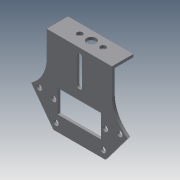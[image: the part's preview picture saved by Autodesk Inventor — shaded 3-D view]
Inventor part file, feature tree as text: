
AUTODESK INVENTOR PART (.ipt)
format: ipt  version: 2013 (Build 170138000, 138)  size: 1,016,832 bytes
history: native  units: mm
features: sketch x90, extrude x79, fillet x2
ambient origin geometry x8: Origin, YZ Plane, XZ Plane, XY Plane, X Axis, Y Axis, Z Axis, Center Point
bodies: Solid1 (feature_tree)
feature tree (171):
  extrude  "Extrusion1"  Depth=10.0mm
  extrude  "Extrusion2"  Depth=10.0mm
  sketch  "Sketch3"  dims[d8=2.0mm d9=0.0mm d11=3.0mm]
  extrude  "Extrusion3"  Depth=3.0mm
  extrude  "Extrusion4"  Depth=3.0mm
  extrude  "Extrusion5"  Depth=10.0mm TaperAngle=0.0deg
  extrude  "Extrusion6"  Depth=3.0mm
  sketch  "Sketch8"  dims[d24=10.0mm d25=0.0mm d26=2.0mm d27=0.0mm]
  extrude  "Extrusion7"  Depth=3.0mm
  extrude  "Extrusion8"  Depth=2.0mm TaperAngle=0.0deg
  extrude  "Extrusion9"  Depth=3.0mm
  extrude  "Extrusion10"  Depth=2.0mm TaperAngle=0.0deg
  extrude  "Extrusion11"  Depth=4.0mm
  extrude  "Extrusion12"  Depth=4.0mm
  extrude  "Extrusion13"  Depth=1.8mm
  sketch  "Sketch16"  dims[d61=4.0mm d62=4.0mm]
  extrude  "Extrusion14"  Depth=4.0mm
  extrude  "Extrusion15"  Depth=12.0mm
  extrude  "Extrusion16"  Depth=4.0mm
  extrude  "Extrusion17"  Depth=16.0mm
  sketch  "Sketch21"  dims[d75=30.0mm d77=2.0mm d78=0.0mm]
  extrude  "Extrusion18"  Depth=10.4mm
  extrude  "Extrusion19"  Depth=4.0mm
  extrude  "Extrusion20"  Depth=20.0mm
  extrude  "Extrusion21"  Depth=2.0mm TaperAngle=0.0deg
  extrude  "Extrusion22"  Depth=2.3mm
  extrude  "Extrusion23"  Depth=24.0mm
  extrude  "Extrusion24"  Depth=2.0mm TaperAngle=0.0deg
  extrude  "Extrusion25"  Depth=3.0mm
  extrude  "Extrusion26"  Depth=2.0mm TaperAngle=0.0deg
  extrude  "Extrusion27"  Depth=2.0mm TaperAngle=0.0deg
  extrude  "Extrusion28"  Depth=4.0mm
  extrude  "Extrusion29"  Depth=3.0mm
  extrude  "Extrusion30"  Depth=3.0mm
  extrude  "Extrusion31"  Depth=3.0mm
  extrude  "Extrusion32"  Depth=4.0mm
  extrude  "Extrusion33"  Depth=3.0mm
  extrude  "Extrusion34"  Depth=2.0mm TaperAngle=0.0deg
  extrude  "Extrusion35"  Depth=2.3mm
  extrude  "Extrusion36"  Depth=4.0mm
  extrude  "Extrusion37"  Depth=2.3mm
  sketch  "Sketch42"  dims[d147=24.0mm d148=24.0mm]
  sketch  "Sketch43"  dims[d149=2.0mm d150=0.0mm d151=2.0mm d152=0.0mm]
  extrude  "Extrusion38"  Depth=2.0mm TaperAngle=0.0deg
  extrude  "Extrusion39"  Depth=2.0mm TaperAngle=0.0deg
  extrude  "Extrusion40"  Depth=20.0mm
  extrude  "Extrusion41"  Depth=20.0mm
  extrude  "Extrusion42"  Depth=24.0mm
  extrude  "Extrusion43"  Depth=2.0mm TaperAngle=0.0deg
  extrude  "Extrusion44"  Depth=3.0mm
  extrude  "Extrusion45"  Depth=20.0mm
  extrude  "Extrusion46"  Depth=2.0mm TaperAngle=0.0deg
  extrude  "Extrusion47"  Depth=3.0mm
  extrude  "Extrusion48"  Depth=3.0mm
  fillet  "Fillet1"  Radius=3.0mm
  extrude  "Extrusion49"  Depth=2.5mm
  fillet  "Fillet2"  Radius=2.0mm
  extrude  "Extrusion50"  Depth=12.5mm
  extrude  "Extrusion51"  Depth=2.5mm
  extrude  "Extrusion52"  Depth=20.0mm
  extrude  "Extrusion53"  Depth=25.0mm
  extrude  "Extrusion54"  Depth=2.0mm TaperAngle=0.0deg
  extrude  "Extrusion55"  Depth=1.5mm
  extrude  "Extrusion56"  Depth=20.0mm
  extrude  "Extrusion57"  Depth=20.0mm
  extrude  "Extrusion58"  Depth=24.0mm
  extrude  "Extrusion59"  Depth=3.4mm
  extrude  "Extrusion60"  Depth=3.0mm
  extrude  "Extrusion61"  Depth=3.0mm
  extrude  "Extrusion62"  Depth=2.0mm TaperAngle=0.0deg
  sketch  "Sketch67"  dims[d218=3.0mm d219=3.0mm]
  extrude  "Extrusion63"  Depth=17.0mm
  extrude  "Extrusion64"  Depth=2.0mm TaperAngle=0.0deg
  extrude  "Extrusion65"  Depth=14.4mm
  sketch  "Sketch71"  dims[d228=1.5mm d229=3.0mm]
  sketch  "Sketch72"  dims[d230=2.0mm d231=0.0mm d233=2.0mm d234=0.0mm]
  extrude  "Extrusion66"  Depth=1.5mm
  sketch  "Sketch73"  dims[d236=14.5mm d237=13.95mm]
  sketch  "Sketch74"  dims[d238=13.95mm d239=3.0mm]
  extrude  "Extrusion67"  Depth=3.0mm
  extrude  "Extrusion68"  Depth=2.0mm TaperAngle=0.0deg
  extrude  "Extrusion69"  Depth=1.5mm
  extrude  "Extrusion70"  Depth=14.4mm
  extrude  "Extrusion71"  Depth=3.0mm
  sketch  "Sketch80"  dims[d256=19.0mm]
  sketch  "Sketch81"  dims[d259=19.0mm]
  extrude  "Extrusion72"  Depth=2.0mm TaperAngle=0.0deg
  extrude  "Extrusion73"  Depth=13.95mm
  sketch  "Sketch84"  dims[d263=4.0mm]
  extrude  "Extrusion74"  Depth=3.0mm
  extrude  "Extrusion75"  Depth=2.0mm TaperAngle=0.0deg
  extrude  "Extrusion76"  Depth=14.4mm
  extrude  "Extrusion77"  Depth=2.0mm
  extrude  "Extrusion78"  Depth=4.0mm
  extrude  "Extrusion79"  Depth=2.0mm TaperAngle=0.0deg
  sketch  "Sketch1"  dims[d2=10.0mm d3=10.0mm]
  sketch  "Sketch2"  dims[d4=10.0mm d7=10.0mm]
  sketch  "Sketch4"  dims[d12=3.0mm d14=3.0mm]
  sketch  "Sketch5"  dims[d15=3.0mm d16=10.0mm d17=0.0mm]
  sketch  "Sketch6"  dims[d20=6.0mm d21=3.0mm]
  sketch  "Sketch7"  dims[d22=6.0mm d23=3.0mm]
  sketch  "Sketch9"  dims[d34=3.0mm d36=3.0mm]
  sketch  "Sketch10"  dims[d37=2.0mm d38=0.0mm d39=2.0mm d40=0.0mm]
  sketch  "Sketch11"  dims[d48=2.0mm d49=4.0mm]
  sketch  "Sketch12"  dims[d51=12.0mm d52=4.0mm]
  sketch  "Sketch13"  dims[d53=2.0mm d54=0.0mm d55=1.8mm]
  sketch  "Sketch14"  dims[d56=2.0mm d57=4.0mm]
  sketch  "Sketch15"  dims[d58=2.0mm d59=0.0mm d60=12.0mm]
  sketch  "Sketch17"  dims[d63=2.0mm d64=0.0mm d65=16.0mm]
  sketch  "Sketch18"  dims[d66=12.0mm d67=10.4mm]
  sketch  "Sketch19"  dims[d68=2.0mm d69=0.0mm d70=4.0mm]
  sketch  "Sketch20"  dims[d71=2.0mm d72=0.0mm d74=20.0mm]
  sketch  "Sketch22"  dims[d83=2.3mm d84=2.3mm]
  sketch  "Sketch23"  dims[d85=2.0mm d86=0.0mm d90=24.0mm]
  sketch  "Sketch24"  dims[d92=24.0mm d93=2.0mm d94=0.0mm]
  sketch  "Sketch25"  dims[d97=3.0mm d98=3.0mm]
  sketch  "Sketch26"  dims[d100=3.0mm d101=2.0mm d102=0.0mm]
  sketch  "Sketch27"  dims[d103=2.0mm d104=0.0mm d105=2.0mm d106=0.0mm]
  sketch  "Sketch28"  dims[d111=4.0mm d112=4.0mm]
  sketch  "Sketch29"  dims[d113=3.0mm d114=3.0mm]
  sketch  "Sketch30"  dims[d116=3.0mm d117=3.0mm]
  sketch  "Sketch31"  dims[d118=3.0mm d119=3.0mm]
  sketch  "Sketch32"  dims[d120=3.0mm d121=4.0mm]
  sketch  "Sketch33"  dims[d122=3.0mm d123=3.0mm]
  sketch  "Sketch34"  dims[d124=3.0mm d125=2.0mm d126=0.0mm]
  sketch  "Sketch35"  dims[d127=2.3mm d128=2.3mm]
  sketch  "Sketch36"  dims[d131=4.0mm d132=4.0mm]
  sketch  "Sketch37"  dims[d133=2.0mm d134=0.0mm d135=2.3mm]
  sketch  "Sketch38"  dims[d136=2.3mm d137=2.0mm d138=0.0mm]
  sketch  "Sketch39"  dims[d139=3.0mm d140=2.0mm d141=0.0mm]
  sketch  "Sketch40"  dims[d142=2.0mm d143=0.0mm d144=20.0mm]
  sketch  "Sketch41"  dims[d145=14.0mm d146=20.0mm]
  sketch  "Sketch44"  dims[d157=3.0mm d158=3.0mm]
  sketch  "Sketch45"  dims[d159=2.0mm d160=0.0mm d161=20.0mm]
  sketch  "Sketch46"  dims[d162=20.0mm d163=2.0mm d164=0.0mm]
  sketch  "Sketch47"  dims[d165=2.0mm d166=0.0mm d167=3.0mm]
  sketch  "Sketch48"  dims[d168=3.0mm d169=3.0mm d170=3.0mm]
  sketch  "Sketch49"  dims[d171=2.5mm d172=2.5mm d173=2.0mm d174=0.0mm]
  sketch  "Sketch50"  dims[d175=2.0mm d176=0.0mm d178=12.5mm]
  sketch  "Sketch51"  dims[d179=12.5mm d180=2.5mm]
  sketch  "Sketch52"  dims[d181=2.5mm d183=20.0mm]
  sketch  "Sketch53"  dims[d185=20.0mm d186=25.0mm]
  sketch  "Sketch54"  dims[d187=25.0mm d188=2.0mm d189=0.0mm]
  sketch  "Sketch55"  dims[d190=1.5mm d191=1.5mm]
  sketch  "Sketch56"  dims[d192=1.5mm d193=20.0mm]
  sketch  "Sketch57"  dims[d194=1.5mm d195=20.0mm]
  sketch  "Sketch58"  dims[d196=24.0mm d197=24.0mm]
  sketch  "Sketch59"  dims[d198=2.0mm d199=0.0mm d200=3.4mm]
  sketch  "Sketch60"  dims[d201=3.4mm d202=3.0mm]
  sketch  "Sketch61"  dims[d203=3.0mm d204=3.0mm]
  sketch  "Sketch62"  dims[d205=3.0mm d206=2.0mm d207=0.0mm]
  sketch  "Sketch63"  dims[d208=2.0mm d209=0.0mm d210=17.0mm]
  sketch  "Sketch64"  dims[d211=14.4mm d212=2.0mm d213=0.0mm]
  sketch  "Sketch65"  dims[d214=19.5mm d215=14.4mm]
  sketch  "Sketch66"  dims[d216=1.5mm d217=1.5mm]
  sketch  "Sketch68"  dims[d220=2.0mm d221=0.0mm d222=2.0mm d223=0.0mm]
  sketch  "Sketch69"  dims[d224=19.5mm d225=1.5mm]
  sketch  "Sketch70"  dims[d226=3.0mm d227=14.4mm]
  sketch  "Sketch75"  dims[d241=3.0mm d242=2.0mm d243=0.0mm]
  sketch  "Sketch76"  dims[d244=2.0mm d245=0.0mm d248=14.4mm]
  sketch  "Sketch77"  dims[d249=21.6mm d250=2.0mm]
  sketch  "Sketch78"  dims[d251=2.0mm d252=4.0mm]
  sketch  "Sketch79"  dims[d253=4.0mm d254=2.0mm d255=0.0mm]
  sketch  "Sketch82"  dims[d260=2.0mm d261=0.0mm]
  sketch  "Sketch83"  dims[d262=10.0mm]
  sketch  "Sketch85"  dims[d264=4.0mm]
  sketch  "Sketch86"  dims[d265=2.0mm d266=0.0mm]
  sketch  "Sketch87"  dims[d267=2.0mm d268=0.0mm]
  sketch  "Sketch88"  dims[d269=2.0mm d270=0.0mm]
  sketch  "Sketch89"  dims[d271=2.0mm d272=0.0mm]
  sketch  "Sketch90"  dims[d273=3.6mm d274=2.0mm d275=0.0mm d276=1.5mm d277=10.0mm d278=0.0mm d279=2.0mm d280=0.5mm d281=0.0mm d282=0.5mm d283=1.5mm d284=0.0mm d285=1.5mm d286=0.0mm d287=10.4mm d288=14.398895mm d289=16.0mm d290=1.5mm d291=0.0mm d292=1.5mm d293=0.0mm d294=10.0mm d295=0.0mm d296=10.0mm d297=0.0mm d298=10.0mm d299=0.0mm d300=20.0mm d301=0.0mm d306=1.5mm d307=0.0mm d308=4.0mm d309=7.0mm d310=16.0mm d311=3.0mm d312=7.0mm d313=16.0mm d314=1.5mm d315=0.0mm d316=5.0mm d317=1.5mm d318=0.0mm d319=1.5mm d320=10.0mm d321=0.0mm d322=7.0mm d323=7.0mm d324=4.0mm d325=7.0mm d326=4.0mm d327=7.0mm d328=4.0mm d329=1.5mm d330=0.0mm d331=4.0mm d332=4.129mm d333=7.0mm d335=3.072mm d336=7.0mm d337=15.0mm d338=1.5mm d339=0.0mm d341=1.5mm d342=0.0mm d343=0.5mm d344=7.0mm d345=18.0mm d346=7.0mm d347=1.5mm d348=0.0mm d349=7.0mm d351=7.0mm d353=1.5mm d354=0.0mm d359=8.3mm d360=11.6mm d361=23.6mm d362=12.4mm d363=1.5mm d364=0.0mm d365=27.9mm d366=0.4mm d367=1.5mm d368=0.0mm d370=0.3mm d371=0.3mm d372=1.5mm d373=0.0mm d374=5.0mm d375=5.0mm d376=1.5mm d377=0.0mm d378=6.3mm d379=12.6mm d380=3.0mm d381=3.0mm d382=1.5mm d383=0.0mm d391=1.5mm d392=0.0mm d395=7.0mm d396=19.0mm d399=7.0mm d400=1.5mm d401=0.0mm d403=1.5mm d404=0.0mm d406=1.5mm d407=3.0mm d409=1.5mm d410=3.0mm d411=1.5mm d412=0.0mm d413=14.5mm d414=3.0mm d415=1.5mm d416=0.0mm d417=3.0mm d418=1.5mm d419=3.0mm d420=2.0mm d421=3.0mm d422=3.0mm d423=1.5mm d424=0.0mm d425=1.5mm d426=1.5mm d427=0.0mm d428=1.5mm d429=1.5mm d430=0.0mm]
